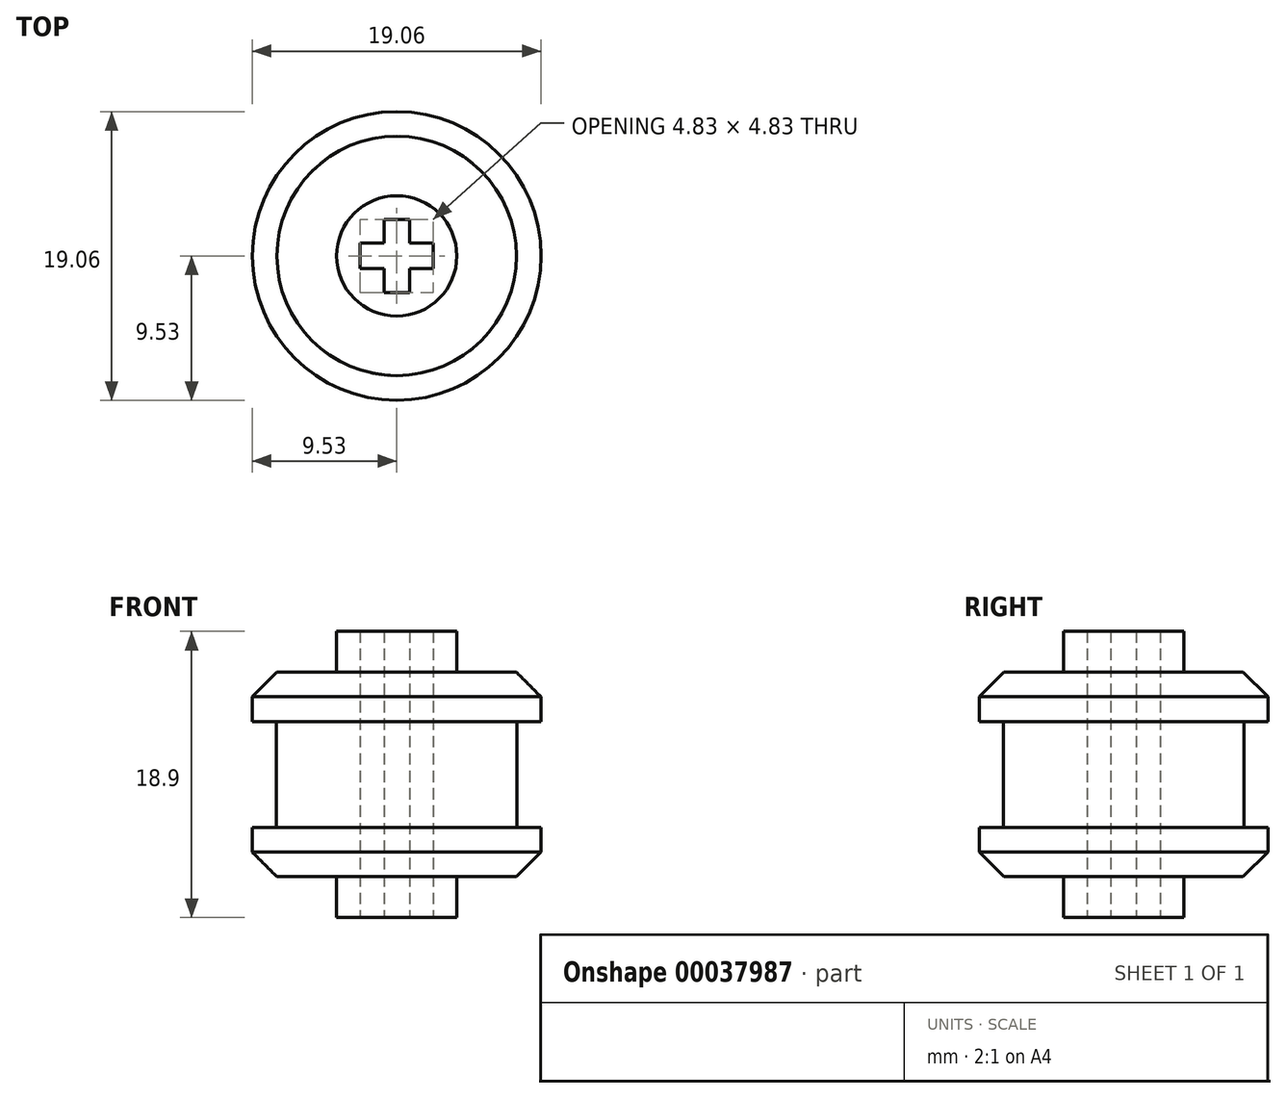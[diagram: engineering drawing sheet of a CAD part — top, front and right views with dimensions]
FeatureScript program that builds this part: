
annotation { "Feature Type Name" : "Feature", "Feature Type Description" : "" }
export const myFeature = defineFeature(function(context is Context, id is Id, definition is map)
    precondition{}
    {
        {
            var Q0;
            Q0=qCreatedBy(makeId("Top.planeOp"),FACE);
            var sketch = newSketch(context, id + "F0", { "sketchPlane" : qUnion([Q0])});
            skCircle(sketch, "E0", {"center": v(0, 0) * mm, "radius": 7.94 * mm});
            skLineSegment(sketch, "E1.rect.bottom", {"start": v(2.41, 0.84) * mm, "end": v(-2.41, 0.84) * mm});
            skLineSegment(sketch, "E1.rect.top", {"start": v(2.41, -0.84) * mm, "end": v(-2.41, -0.84) * mm});
            skLineSegment(sketch, "E1.rect.left", {"start": v(2.41, 0.84) * mm, "end": v(2.41, -0.84) * mm});
            skLineSegment(sketch, "E1.rect.right", {"start": v(-2.41, 0.84) * mm, "end": v(-2.41, -0.84) * mm});
            skLineSegment(sketch, "E2.rect.bottom", {"start": v(0.84, -2.41) * mm, "end": v(-0.84, -2.41) * mm});
            skLineSegment(sketch, "E2.rect.top", {"start": v(0.84, 2.41) * mm, "end": v(-0.84, 2.41) * mm});
            skLineSegment(sketch, "E2.rect.left", {"start": v(0.84, -2.41) * mm, "end": v(0.84, 2.41) * mm});
            skLineSegment(sketch, "E2.rect.right", {"start": v(-0.84, -2.41) * mm, "end": v(-0.84, 2.41) * mm});
            skSolve(sketch);
        }
        {
            var Q0;
            Q0=qSketchRegion(id+"F0",true);
            extrude(context, id + "F1", {"entities" : qUnion([Q0]), "depth" : 7 * mm});
        }
        {
            var Q0;
            Q0=makeQuery(id+"F1.opExtrude","CAP_FACE",FACE,{"disambiguationData":[OSD([sQuery(id+"F0.wireOp",EDGE,"E0"),sQuery(id+"F0.wireOp",EDGE,"E1.rect.bottom"),sQuery(id+"F0.wireOp",EDGE,"E1.rect.top"),sQuery(id+"F0.wireOp",EDGE,"E1.rect.left"),sQuery(id+"F0.wireOp",EDGE,"E1.rect.right"),sQuery(id+"F0.wireOp",EDGE,"E2.rect.bottom"),sQuery(id+"F0.wireOp",EDGE,"E2.rect.top"),sQuery(id+"F0.wireOp",EDGE,"E2.rect.left"),sQuery(id+"F0.wireOp",EDGE,"E2.rect.right")])],"isStart":false});
            var sketch = newSketch(context, id + "F2", { "sketchPlane" : qUnion([Q0])});
            skCircle(sketch, "E3", {"center": v(0, 0) * mm, "radius": 9.53 * mm});
            skSolve(sketch);
        }
        {
            var Q0;
            Q0=makeQuery(id+"F2.imprint","IMPRINT",FACE,{"disambiguationData":[TD([[makeQuery(id+"F2.imprint","IMPRINT",EDGE,{"derivedFrom":sQuery(id+"F2.wireOp",EDGE,"E3")}),1.0]])]});
            var Q1;
            Q1=makeQuery(id+"F2.imprint","IMPRINT",FACE,{"disambiguationData":[TD([[makeQuery(id+"F2.imprint","IMPRINT",EDGE,{"derivedFrom":makeQuery(id+"F1.opExtrude","CAP_EDGE",EDGE,{"disambiguationData":[OSD([sQuery(id+"F0.wireOp",EDGE,"E0")])],"isStart":false})}),1.0]])]});
            extrude(context, id + "F3", {"entities" : qUnion([Q0, Q1]), "operationType" : NewBodyOperationType.ADD, "depth" : 3.25 * mm});
        }
        {
            var Q0;
            Q0=makeQuery(id+"F1.opExtrude","CAP_FACE",FACE,{"disambiguationData":[OSD([sQuery(id+"F0.wireOp",EDGE,"E0"),sQuery(id+"F0.wireOp",EDGE,"E1.rect.bottom"),sQuery(id+"F0.wireOp",EDGE,"E1.rect.top"),sQuery(id+"F0.wireOp",EDGE,"E1.rect.left"),sQuery(id+"F0.wireOp",EDGE,"E1.rect.right"),sQuery(id+"F0.wireOp",EDGE,"E2.rect.bottom"),sQuery(id+"F0.wireOp",EDGE,"E2.rect.top"),sQuery(id+"F0.wireOp",EDGE,"E2.rect.left"),sQuery(id+"F0.wireOp",EDGE,"E2.rect.right")])],"isStart":true});
            var sketch = newSketch(context, id + "F4", { "sketchPlane" : qUnion([Q0])});
            skCircle(sketch, "E4", {"center": v(0, 0) * mm, "radius": 9.53 * mm});
            skSolve(sketch);
        }
        {
            var Q0;
            Q0=makeQuery(id+"F4.imprint","IMPRINT",FACE,{"disambiguationData":[TD([[makeQuery(id+"F4.imprint","IMPRINT",EDGE,{"derivedFrom":sQuery(id+"F4.wireOp",EDGE,"E4")}),1.0]])]});
            var Q1;
            Q1=makeQuery(id+"F4.imprint","IMPRINT",FACE,{"disambiguationData":[TD([[makeQuery(id+"F4.imprint","IMPRINT",EDGE,{"derivedFrom":makeQuery(id+"F1.opExtrude","CAP_EDGE",EDGE,{"disambiguationData":[OSD([sQuery(id+"F0.wireOp",EDGE,"E0")])],"isStart":true})}),-1.0]])]});
            extrude(context, id + "F5", {"entities" : qUnion([Q0, Q1]), "operationType" : NewBodyOperationType.ADD, "depth" : 3.25 * mm});
        }
        {
            var Q0;
            Q0=makeQuery(id+"F3.opExtrude","CAP_EDGE",EDGE,{"disambiguationData":[OSD([sQuery(id+"F2.wireOp",EDGE,"E3")])],"isStart":false});
            var Q1;
            Q1=makeQuery(id+"F5.opExtrude","CAP_EDGE",EDGE,{"disambiguationData":[OSD([sQuery(id+"F4.wireOp",EDGE,"E4")])],"isStart":false});
            chamfer(context, id + "F6", {"entities" : qUnion([Q0, Q1]), "width" : 1.63 * mm, "tangentPropagation" : true});
        }
        {
            var Q0;
            Q0=makeQuery(id+"F3.opExtrude","CAP_FACE",FACE,{"disambiguationData":[OSD([sQuery(id+"F0.wireOp",EDGE,"E1.rect.bottom"),sQuery(id+"F0.wireOp",EDGE,"E1.rect.top"),sQuery(id+"F0.wireOp",EDGE,"E1.rect.left"),sQuery(id+"F0.wireOp",EDGE,"E1.rect.right"),sQuery(id+"F0.wireOp",EDGE,"E2.rect.bottom"),sQuery(id+"F0.wireOp",EDGE,"E2.rect.top"),sQuery(id+"F0.wireOp",EDGE,"E2.rect.left"),sQuery(id+"F0.wireOp",EDGE,"E2.rect.right"),sQuery(id+"F2.wireOp",EDGE,"E3")])],"isStart":false});
            var sketch = newSketch(context, id + "F7", { "sketchPlane" : qUnion([Q0])});
            skCircle(sketch, "E5", {"center": v(0, 0) * mm, "radius": 3.97 * mm});
            skSolve(sketch);
        }
        {
            var Q0;
            Q0=makeQuery(id+"F7.imprint","IMPRINT",FACE,{"disambiguationData":[TD([[makeQuery(id+"F7.imprint","IMPRINT",EDGE,{"derivedFrom":sQuery(id+"F7.wireOp",EDGE,"E5")}),1.0]])]});
            extrude(context, id + "F8", {"entities" : qUnion([Q0]), "operationType" : NewBodyOperationType.ADD, "depth" : 2.7 * mm});
        }
        {
            var Q0;
            Q0=makeQuery(id+"F5.opExtrude","CAP_FACE",FACE,{"disambiguationData":[OSD([sQuery(id+"F0.wireOp",EDGE,"E1.rect.bottom"),sQuery(id+"F0.wireOp",EDGE,"E1.rect.top"),sQuery(id+"F0.wireOp",EDGE,"E1.rect.left"),sQuery(id+"F0.wireOp",EDGE,"E1.rect.right"),sQuery(id+"F0.wireOp",EDGE,"E2.rect.bottom"),sQuery(id+"F0.wireOp",EDGE,"E2.rect.top"),sQuery(id+"F0.wireOp",EDGE,"E2.rect.left"),sQuery(id+"F0.wireOp",EDGE,"E2.rect.right"),sQuery(id+"F4.wireOp",EDGE,"E4")])],"isStart":false});
            var sketch = newSketch(context, id + "F9", { "sketchPlane" : qUnion([Q0])});
            skCircle(sketch, "E6", {"center": v(0, 0) * mm, "radius": 3.97 * mm});
            skSolve(sketch);
        }
        {
            var Q0;
            Q0=makeQuery(id+"F9.imprint","IMPRINT",FACE,{"disambiguationData":[TD([[makeQuery(id+"F9.imprint","IMPRINT",EDGE,{"derivedFrom":sQuery(id+"F9.wireOp",EDGE,"E6")}),1.0]])]});
            extrude(context, id + "F10", {"entities" : qUnion([Q0]), "operationType" : NewBodyOperationType.ADD, "depth" : 2.7 * mm});
        }
    });
